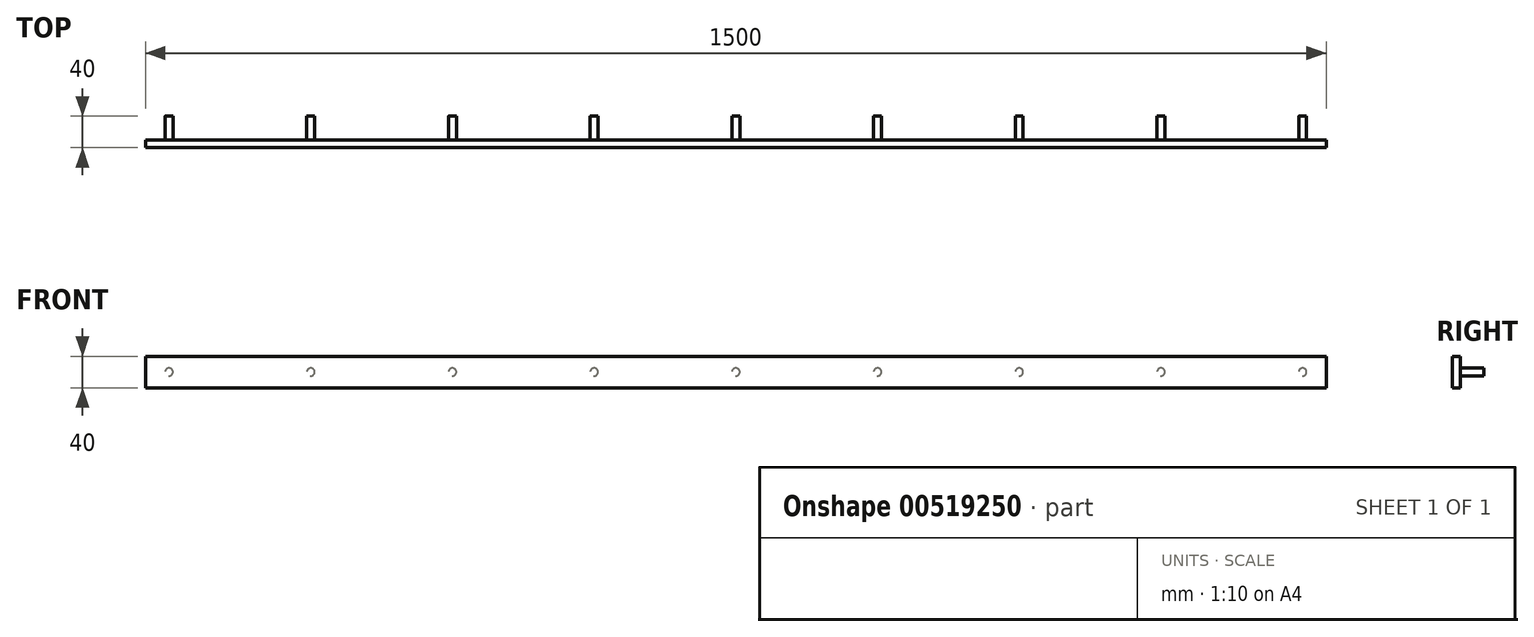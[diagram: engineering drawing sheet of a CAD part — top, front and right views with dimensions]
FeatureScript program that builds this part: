
annotation { "Feature Type Name" : "Feature", "Feature Type Description" : "" }
export const myFeature = defineFeature(function(context is Context, id is Id, definition is map)
    precondition{}
    {
        {
            var Q0;
            Q0=qCreatedBy(makeId("Right.planeOp"),FACE);
            var sketch = newSketch(context, id + "F0", { "sketchPlane" : qUnion([Q0])});
            skLineSegment(sketch, "E0.bottom", {"start": v(0, 0) * mm, "end": v(10, 0) * mm});
            skLineSegment(sketch, "E0.top", {"start": v(0, 40) * mm, "end": v(10, 40) * mm});
            skLineSegment(sketch, "E0.left", {"start": v(0, 0) * mm, "end": v(0, 40) * mm});
            skLineSegment(sketch, "E0.right", {"start": v(10, 0) * mm, "end": v(10, 40) * mm});
            skSolve(sketch);
        }
        {
            var Q0;
            Q0 = qSketchRegion(id + "F0", true);
            extrude(context, id + "F1", {"entities" : qUnion([Q0]), "oppositeDirection" : true, "depth" : 1500 * mm, "offsetDistance" : 25 * mm});
        }
        {
            var Q0;
            Q0=makeQuery(id+"F1.opExtrude","SWEPT_FACE",FACE,{"disambiguationData":[OSD([sQuery(id+"F0.wireOp",EDGE,"E0.right")])]});
            var sketch = newSketch(context, id + "F2", { "sketchPlane" : qUnion([Q0])});
            skCircle(sketch, "E1", {"center": v(30, 20) * mm, "radius": 5 * mm});
            skPoint(sketch, "E1.centerSnap0", {"position": v(0, 20) * mm});
            skCircle(sketch, "E2.1.0.0", {"center": v(210, 20) * mm, "radius": 5 * mm});
            skCircle(sketch, "E2.2.0.0", {"center": v(390, 20) * mm, "radius": 5 * mm});
            skCircle(sketch, "E2.3.0.0", {"center": v(570, 20) * mm, "radius": 5 * mm});
            skCircle(sketch, "E2.4.0.0", {"center": v(750, 20) * mm, "radius": 5 * mm});
            skCircle(sketch, "E2.5.0.0", {"center": v(930, 20) * mm, "radius": 5 * mm});
            skCircle(sketch, "E2.6.0.0", {"center": v(1110, 20) * mm, "radius": 5 * mm});
            skCircle(sketch, "E2.7.0.0", {"center": v(1290, 20) * mm, "radius": 5 * mm});
            skCircle(sketch, "E2.8.0.0", {"center": v(1470, 20) * mm, "radius": 5 * mm});
            skLineSegment(sketch, "E2.direction1", {"start": v(30, 20) * mm, "end": v(210, 20) * mm, "construction": true});
            skSolve(sketch);
        }
        {
            var Q0;
            Q0 = qSketchRegion(id + "F2", true);
            extrude(context, id + "F3", {"entities" : qUnion([Q0]), "operationType" : NewBodyOperationType.ADD, "depth" : 30 * mm, "offsetDistance" : 25 * mm});
        }
    });
